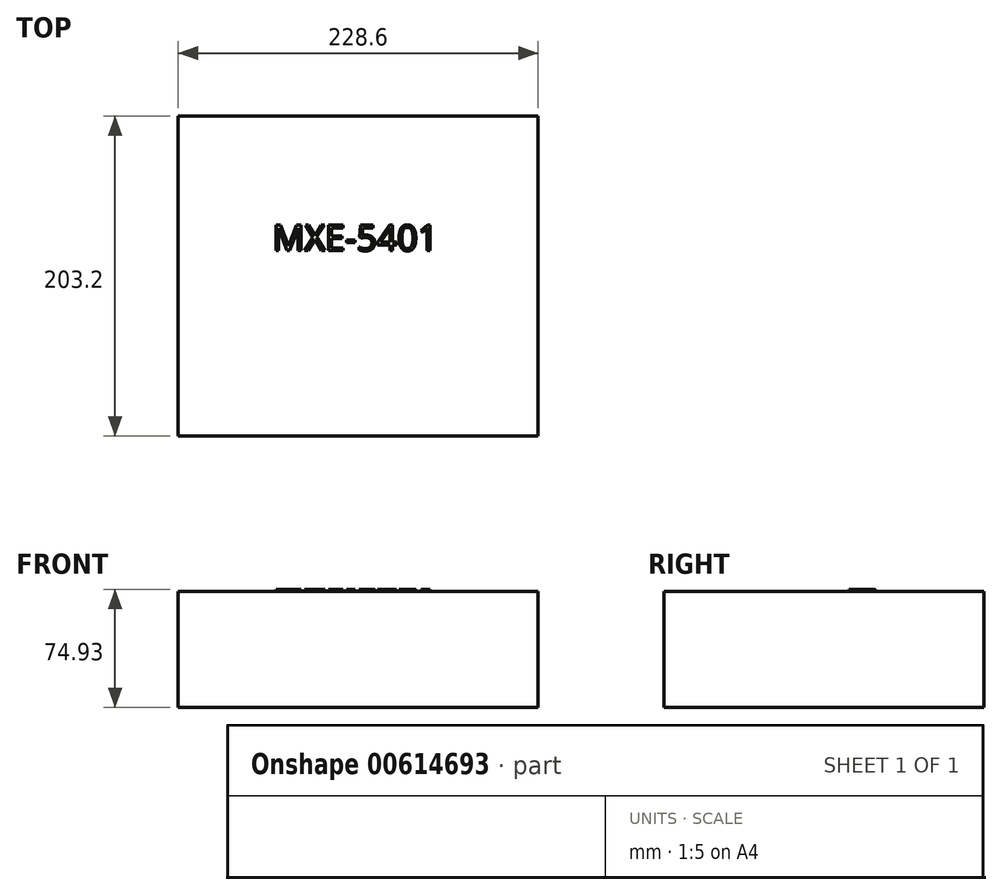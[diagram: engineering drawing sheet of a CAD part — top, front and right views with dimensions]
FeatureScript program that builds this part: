
annotation { "Feature Type Name" : "Feature", "Feature Type Description" : "" }
export const myFeature = defineFeature(function(context is Context, id is Id, definition is map)
    precondition{}
    {
        {
            var Q0;
            Q0=qCreatedBy(makeId("Top.planeOp"),FACE);
            var sketch = newSketch(context, id + "F0", { "sketchPlane" : qUnion([Q0])});
            skLineSegment(sketch, "E0.bottom", {"start": v(-103.59, 137.33) * mm, "end": v(125.01, 137.33) * mm});
            skLineSegment(sketch, "E0.top", {"start": v(-103.59, -65.87) * mm, "end": v(125.01, -65.87) * mm});
            skLineSegment(sketch, "E0.left", {"start": v(-103.59, 137.33) * mm, "end": v(-103.59, -65.87) * mm});
            skLineSegment(sketch, "E0.right", {"start": v(125.01, 137.33) * mm, "end": v(125.01, -65.87) * mm});
            skSolve(sketch);
        }
        {
            var Q0;
            Q0=makeQuery(id+"F0.imprint","IMPRINT",FACE,{"disambiguationData":[TD([[makeQuery(id+"F0.imprint","IMPRINT",EDGE,{"derivedFrom":sQuery(id+"F0.wireOp",EDGE,"E0.bottom")}),-1.0]])]});
            extrude(context, id + "F1", {"entities" : qUnion([Q0]), "depth" : 73.66 * mm, "offsetDistance" : 25.4 * mm});
        }
        {
            var Q0;
            Q0=makeQuery(id+"F1.opExtrude","CAP_FACE",FACE,{"disambiguationData":[OSD([sQuery(id+"F0.wireOp",EDGE,"E0.bottom"),sQuery(id+"F0.wireOp",EDGE,"E0.top"),sQuery(id+"F0.wireOp",EDGE,"E0.left"),sQuery(id+"F0.wireOp",EDGE,"E0.right")])],"isStart":false});
            var sketch = newSketch(context, id + "F2", { "sketchPlane" : qUnion([Q0])});
            skText(sketch, "E1", { "text": "MXE-5401", "fontName": "OpenSans-Regular.ttf"});
            const initialGuessF2  = {"E1": [-0.04373, 0.05183, 1, 0, 0.0163]};
            skSetInitialGuess(sketch, initialGuessF2);
            skSolve(sketch);
        }
        {
            var Q0;
            Q0 = qSketchRegion(id + "F2", true);
            extrude(context, id + "F3", {"entities" : qUnion([Q0]), "operationType" : NewBodyOperationType.ADD, "depth" : 1.27 * mm, "offsetDistance" : 25.4 * mm});
        }
    });
